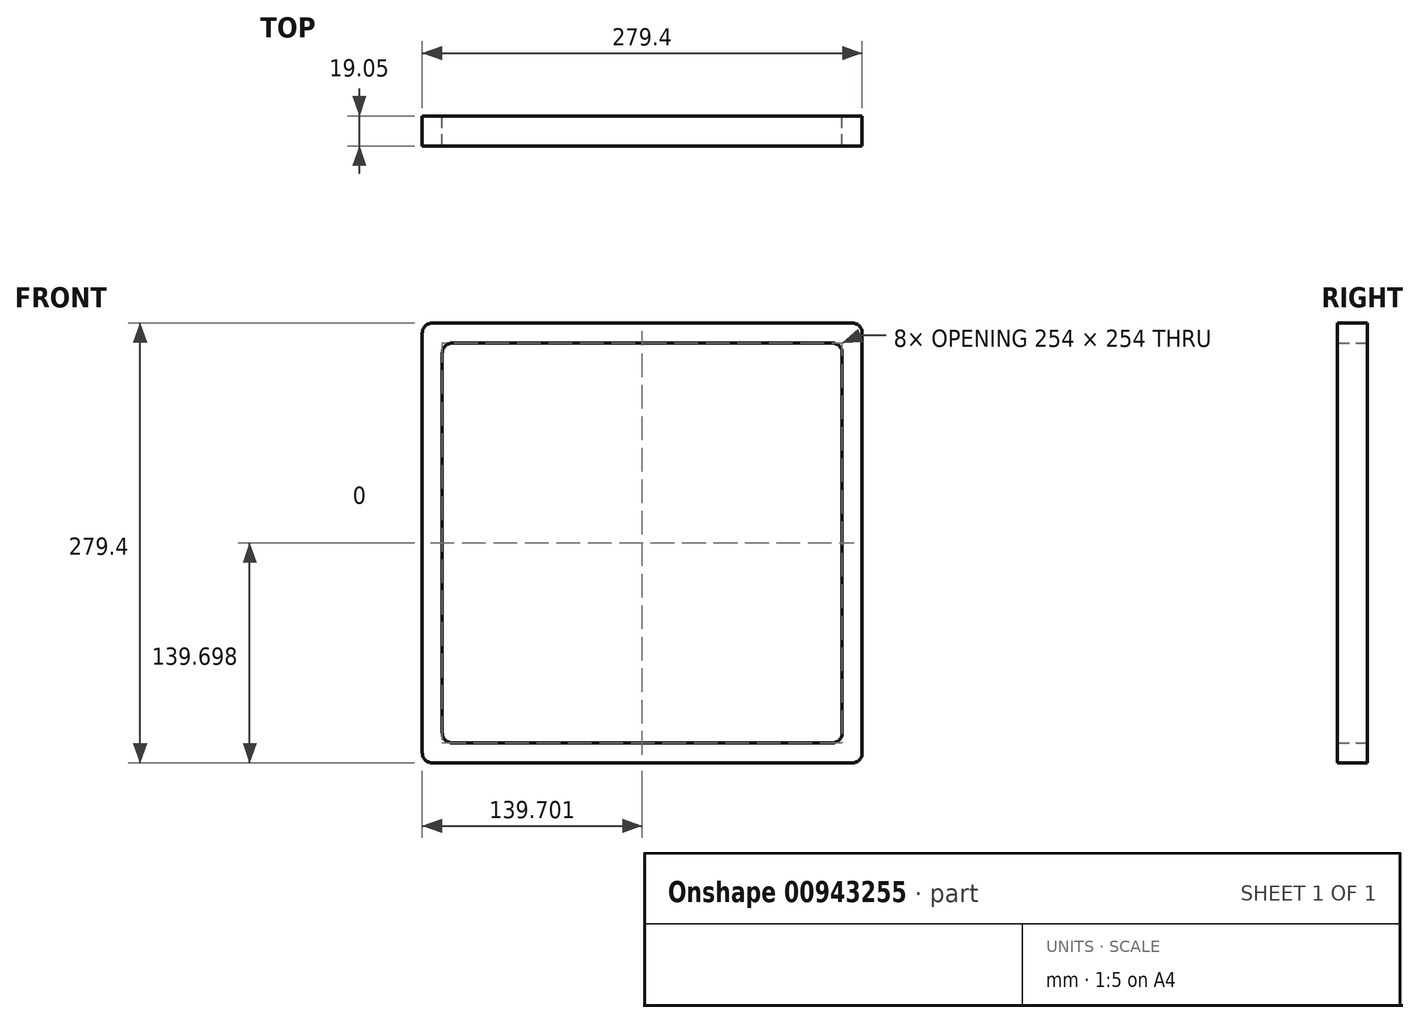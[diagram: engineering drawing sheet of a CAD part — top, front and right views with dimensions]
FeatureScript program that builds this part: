
annotation { "Feature Type Name" : "Feature", "Feature Type Description" : "" }
export const myFeature = defineFeature(function(context is Context, id is Id, definition is map)
    precondition{}
    {
        {
            var Q0;
            Q0=qCreatedBy(makeId("Front.planeOp"),FACE);
            var sketch = newSketch(context, id + "F0", { "sketchPlane" : qUnion([Q0])});
            skLineSegment(sketch, "E0.bottom", {"start": v(-146.5, -145.42) * mm, "end": v(94.8, -145.42) * mm});
            skLineSegment(sketch, "E0.top", {"start": v(-146.5, 108.58) * mm, "end": v(94.8, 108.58) * mm});
            skLineSegment(sketch, "E0.left", {"start": v(-152.85, -139.07) * mm, "end": v(-152.85, 102.23) * mm});
            skLineSegment(sketch, "E0.right", {"start": v(101.15, -139.07) * mm, "end": v(101.15, 102.23) * mm});
            skPoint(sketch, "E1", {"position": v(-121.1, 108.58) * mm});
            skPoint(sketch, "E2", {"position": v(-89.35, 108.58) * mm});
            skPoint(sketch, "E3", {"position": v(-57.6, 108.58) * mm});
            skPoint(sketch, "E4", {"position": v(-25.85, 108.58) * mm});
            skPoint(sketch, "E5", {"position": v(5.9, 108.58) * mm});
            skPoint(sketch, "E6", {"position": v(37.65, 108.58) * mm});
            skPoint(sketch, "E7", {"position": v(69.4, 108.58) * mm});
            skPoint(sketch, "E8", {"position": v(-152.85, 76.83) * mm});
            skPoint(sketch, "E9", {"position": v(-152.85, 45.08) * mm});
            skPoint(sketch, "E10", {"position": v(-152.85, 13.33) * mm});
            skPoint(sketch, "E11", {"position": v(-152.85, -18.42) * mm});
            skPoint(sketch, "E12", {"position": v(-152.85, -50.17) * mm});
            skPoint(sketch, "E13", {"position": v(-152.85, -81.92) * mm});
            skPoint(sketch, "E14", {"position": v(-152.85, -113.67) * mm});
            skLineSegment(sketch, "E15", {"start": v(-121.1, 108.58) * mm, "end": v(-121.1, -145.42) * mm});
            skLineSegment(sketch, "E16", {"start": v(-89.35, 108.58) * mm, "end": v(-89.35, -145.42) * mm});
            skLineSegment(sketch, "E17", {"start": v(-57.6, 108.58) * mm, "end": v(-57.6, -145.42) * mm});
            skLineSegment(sketch, "E18", {"start": v(5.9, 108.58) * mm, "end": v(5.9, -145.42) * mm});
            skLineSegment(sketch, "E19", {"start": v(37.65, 108.58) * mm, "end": v(37.65, -145.42) * mm});
            skLineSegment(sketch, "E20", {"start": v(69.4, 108.58) * mm, "end": v(69.4, -145.42) * mm});
            skLineSegment(sketch, "E21", {"start": v(-152.85, 76.83) * mm, "end": v(101.15, 76.83) * mm});
            skLineSegment(sketch, "E22", {"start": v(-152.85, 45.08) * mm, "end": v(101.15, 45.08) * mm});
            skLineSegment(sketch, "E23", {"start": v(-152.85, 13.33) * mm, "end": v(101.15, 13.33) * mm});
            skLineSegment(sketch, "E24", {"start": v(-25.85, 108.58) * mm, "end": v(-25.85, -145.42) * mm});
            skLineSegment(sketch, "E25", {"start": v(-152.85, -18.42) * mm, "end": v(101.15, -18.42) * mm});
            skLineSegment(sketch, "E26", {"start": v(-152.85, -50.17) * mm, "end": v(101.15, -50.17) * mm});
            skLineSegment(sketch, "E27", {"start": v(-152.85, -81.92) * mm, "end": v(101.15, -81.92) * mm});
            skLineSegment(sketch, "E28", {"start": v(-152.85, -113.67) * mm, "end": v(101.15, -113.67) * mm});
            skLineSegment(sketch, "E29", {"start": v(107.5, -158.12) * mm, "end": v(-159.2, -158.12) * mm});
            skLineSegment(sketch, "E30", {"start": v(-159.2, 121.28) * mm, "end": v(107.5, 121.28) * mm});
            skLineSegment(sketch, "E31", {"start": v(-165.55, 114.93) * mm, "end": v(-165.55, -151.77) * mm});
            skLineSegment(sketch, "E32", {"start": v(113.85, 114.93) * mm, "end": v(113.85, -151.77) * mm});
            skPoint(sketch, "E33.visualSharp", {"position": v(-165.55, -158.12) * mm});
            skArc(sketch, "E33.filletArc", {"start": v(-165.55, -151.77) * mm, "mid": v(-163.69, -156.26) * mm, "end": v(-159.2, -158.12) * mm});
            skPoint(sketch, "E34.visualSharp", {"position": v(113.85, -158.12) * mm});
            skArc(sketch, "E34.filletArc", {"start": v(107.5, -158.12) * mm, "mid": v(112, -156.26) * mm, "end": v(113.85, -151.77) * mm});
            skPoint(sketch, "E35.visualSharp", {"position": v(113.85, 121.28) * mm});
            skArc(sketch, "E35.filletArc", {"start": v(113.85, 114.93) * mm, "mid": v(112, 119.42) * mm, "end": v(107.5, 121.28) * mm});
            skPoint(sketch, "E36.visualSharp", {"position": v(-165.55, 121.28) * mm});
            skArc(sketch, "E36.filletArc", {"start": v(-159.2, 121.28) * mm, "mid": v(-163.69, 119.42) * mm, "end": v(-165.55, 114.93) * mm});
            skPoint(sketch, "E37.visualSharp", {"position": v(-152.85, 108.58) * mm});
            skArc(sketch, "E37.filletArc", {"start": v(-146.5, 108.58) * mm, "mid": v(-150.99, 106.72) * mm, "end": v(-152.85, 102.23) * mm});
            skPoint(sketch, "E38.visualSharp", {"position": v(101.15, 108.58) * mm});
            skArc(sketch, "E38.filletArc", {"start": v(101.15, 102.23) * mm, "mid": v(99.3, 106.72) * mm, "end": v(94.8, 108.58) * mm});
            skPoint(sketch, "E39.visualSharp", {"position": v(101.15, -145.42) * mm});
            skArc(sketch, "E39.filletArc", {"start": v(94.8, -145.42) * mm, "mid": v(99.3, -143.56) * mm, "end": v(101.15, -139.07) * mm});
            skPoint(sketch, "E40.visualSharp", {"position": v(-152.85, -145.42) * mm});
            skArc(sketch, "E40.filletArc", {"start": v(-152.85, -139.07) * mm, "mid": v(-150.99, -143.56) * mm, "end": v(-146.5, -145.42) * mm});
            skSolve(sketch);
        }
        {
            var Q0;
            Q0 = qSketchRegion(id + "F0", true);
            extrude(context, id + "F1", {"entities" : qUnion([Q0]), "depth" : 19.05 * mm, "offsetDistance" : 25.4 * mm});
        }
    });
